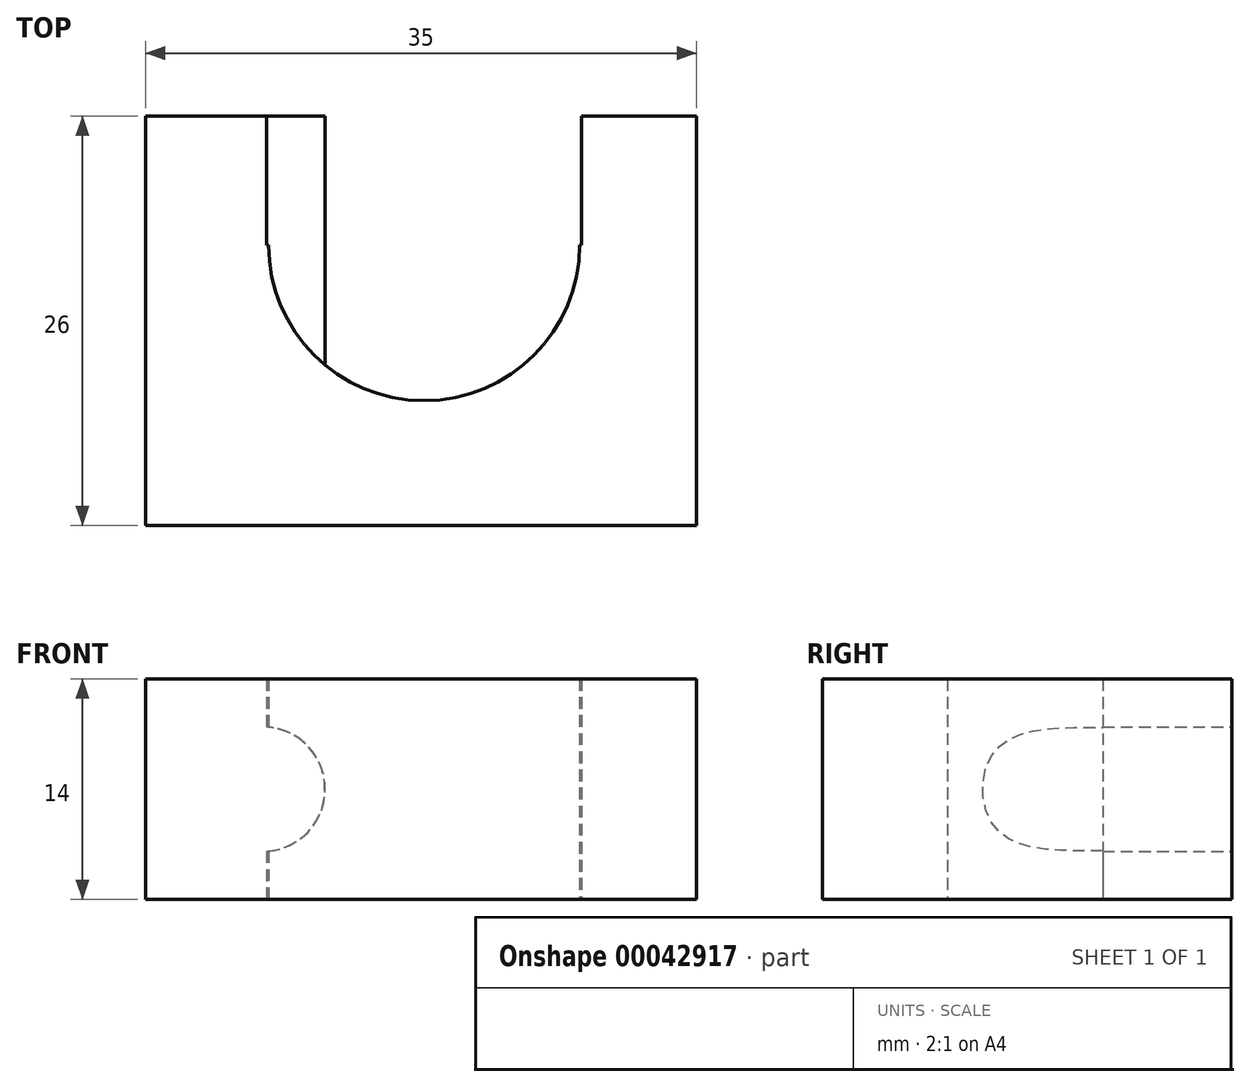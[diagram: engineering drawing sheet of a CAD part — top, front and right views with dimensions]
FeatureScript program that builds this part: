
annotation { "Feature Type Name" : "Feature", "Feature Type Description" : "" }
export const myFeature = defineFeature(function(context is Context, id is Id, definition is map)
    precondition{}
    {
        {
            var Q0;
            Q0=qCreatedBy(makeId("Top.planeOp"),FACE);
            var sketch = newSketch(context, id + "F0", { "sketchPlane" : qUnion([Q0])});
            skLineSegment(sketch, "E0.bottom", {"start": v(14.16, -19.94) * mm, "end": v(-20.84, -19.94) * mm});
            skLineSegment(sketch, "E0.top", {"start": v(14.16, 6.06) * mm, "end": v(-20.84, 6.06) * mm});
            skLineSegment(sketch, "E0.left", {"start": v(14.16, -19.94) * mm, "end": v(14.16, 6.06) * mm});
            skLineSegment(sketch, "E0.right", {"start": v(-20.84, -19.94) * mm, "end": v(-20.84, 6.06) * mm});
            skSolve(sketch);
        }
        {
            var Q0;
            Q0=makeQuery(id+"F0.imprint","IMPRINT",FACE,{"disambiguationData":[TD([[makeQuery(id+"F0.imprint","IMPRINT",EDGE,{"derivedFrom":sQuery(id+"F0.wireOp",EDGE,"E0.bottom")}),-1.0]])]});
            extrude(context, id + "F1", {"entities" : qUnion([Q0]), "depth" : 14 * mm});
        }
        {
            var Q0;
            Q0=makeQuery(id+"F1.opExtrude","CAP_FACE",FACE,{"disambiguationData":[OSD([sQuery(id+"F0.wireOp",EDGE,"E0.bottom"),sQuery(id+"F0.wireOp",EDGE,"E0.top"),sQuery(id+"F0.wireOp",EDGE,"E0.left"),sQuery(id+"F0.wireOp",EDGE,"E0.right")])],"isStart":true});
            var sketch = newSketch(context, id + "F2", { "sketchPlane" : qUnion([Q0])});
            skLineSegment(sketch, "E1.bottom", {"start": v(-13.14, -6.06) * mm, "end": v(6.86, -6.06) * mm});
            skLineSegment(sketch, "E1.top", {"start": v(-13.14, 2.14) * mm, "end": v(6.86, 2.14) * mm});
            skLineSegment(sketch, "E1.left", {"start": v(-13.14, -6.06) * mm, "end": v(-13.14, 2.14) * mm});
            skLineSegment(sketch, "E1.right", {"start": v(6.86, -6.06) * mm, "end": v(6.86, 2.14) * mm});
            skCircle(sketch, "E2", {"center": v(-3.14, 2.14) * mm, "radius": 9.88 * mm});
            skSolve(sketch);
        }
        {
            var Q0;
            Q0=makeQuery(id+"F2.imprint","IMPRINT",FACE,{"disambiguationData":[TD([[makeQuery(id+"F2.imprint","IMPRINT",EDGE,{"derivedFrom":sQuery(id+"F2.wireOp",EDGE,"E1.bottom")}),-1.0]])]});
            var Q1;
            {var subQ0=sQuery(id+"F2.wireOp",EDGE,"E2");var subQ1=sQuery(id+"F2.wireOp",EDGE,"E1.top");var subQ3=makeQuery(id+"F2.imprint","INTERSECT",VERTEX,{"disambiguationData":[OD(0.0)],"derivedFrom":[subQ1,subQ0]});Q1=makeQuery(id+"F2.imprint","IMPRINT",FACE,{"disambiguationData":[TD([[makeQuery(id+"F2.imprint","IMPRINT",EDGE,{"disambiguationData":[TD([[subQ3,-1.0]])],"derivedFrom":subQ1}),-1.0]])]});}
            var Q2;
            {var subQ0=sQuery(id+"F2.wireOp",EDGE,"E2");var subQ1=sQuery(id+"F2.wireOp",EDGE,"E1.top");var subQ3=makeQuery(id+"F2.imprint","INTERSECT",VERTEX,{"disambiguationData":[OD(0.0)],"derivedFrom":[subQ1,subQ0]});Q2=makeQuery(id+"F2.imprint","IMPRINT",FACE,{"disambiguationData":[TD([[makeQuery(id+"F2.imprint","IMPRINT",EDGE,{"disambiguationData":[TD([[subQ3,-1.0]])],"derivedFrom":subQ1}),1.0]])]});}
            extrude(context, id + "F3", {"entities" : qUnion([Q0, Q1, Q2]), "operationType" : NewBodyOperationType.REMOVE, "oppositeDirection" : true, "depth" : 32.63 * mm});
        }
        {
            var Q0;
            {var subQ0=sQuery(id+"F0.wireOp",EDGE,"E0.top");var subQ1=sQuery(id+"F0.wireOp",EDGE,"E0.left");Q0=makeQuery(id+"F3.boolean.opBoolean","SPLIT",FACE,{"disambiguationData":[TD([makeQuery(id+"F1.opExtrude","SWEPT_FACE",FACE,{"disambiguationData":[OSD([subQ1])]})])],"derivedFrom":makeQuery(id+"F1.opExtrude","SWEPT_FACE",FACE,{"disambiguationData":[OSD([subQ0])]})});}
            var sketch = newSketch(context, id + "F4", { "sketchPlane" : qUnion([Q0])});
            skCircle(sketch, "E3", {"center": v(-6.86, 7) * mm, "radius": 3.95 * mm});
            skCircle(sketch, "E4", {"center": v(13.37, 7) * mm, "radius": 3.95 * mm});
            skSolve(sketch);
        }
        {
            var Q0;
            Q0=makeQuery(id+"F4.imprint","IMPRINT",FACE,{"disambiguationData":[TD([[makeQuery(id+"F4.imprint","IMPRINT",EDGE,{"derivedFrom":sQuery(id+"F4.wireOp",EDGE,"E4")}),1.0]])]});
            var Q1;
            {var subQ0=makeQuery(id+"F3.boolean.opBoolean","COPY",EDGE,{"derivedFrom":makeQuery(id+"F3.opExtrude","SWEPT_EDGE",EDGE,{"disambiguationData":[OSD([sQuery(id+"F0.wireOp",EDGE,"E0.top"),sQuery(id+"F2.wireOp",EDGE,"E1.bottom"),sQuery(id+"F2.wireOp",EDGE,"E1.right")])]})});var subQ1=sQuery(id+"F4.wireOp",EDGE,"E3");var subQ3=makeQuery(id+"F4.imprint","INTERSECT",VERTEX,{"disambiguationData":[OD(0.0)],"derivedFrom":[subQ0,subQ1]});Q1=makeQuery(id+"F4.imprint","IMPRINT",FACE,{"disambiguationData":[TD([[makeQuery(id+"F4.imprint","IMPRINT",EDGE,{"disambiguationData":[TD([[subQ3,-1.0]])],"derivedFrom":subQ1}),1.0]])]});}
            extrude(context, id + "F5", {"entities" : qUnion([Q0, Q1]), "operationType" : NewBodyOperationType.ADD, "oppositeDirection" : true, "depth" : 25 * mm});
        }
    });
